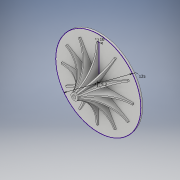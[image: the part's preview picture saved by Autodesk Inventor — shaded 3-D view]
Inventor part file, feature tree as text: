
AUTODESK INVENTOR PART (.ipt)
format: ipt  version: 2019.3 (Build 233278000, 278)  size: 221,696 bytes
history: native  units: mm
features: extrude x4, sketch x3, other x1, pattern_circular x1
ambient origin geometry x8: Origin, YZ Plane, XZ Plane, XY Plane, X Axis, Y Axis, Z Axis, Center Point
bodies: Solid1 (feature_tree)
feature tree (9):
  sketch  "Sketch1"  dims[d0=5.2mm d1=125.0mm]
  extrude  "Extrusion1"  Depth=125.0mm
  extrude  "Extrusion2"  Depth=2.0mm
  other  "Work Axis1"
  extrude  "Extrusion3"  Depth=10.0mm TaperAngle=0.0deg
  pattern_circular  "Circular Pattern1"  [2 undecoded]
  extrude  "Extrusion4"  Depth=2.0mm
  sketch  "Sketch2"  dims[d2=2.0mm d3=1.0mm]
  sketch  "Sketch3"  dims[d4=10.0mm d5=3.0mm d6=0.0mm d7=35.0mm d8=0.0mm d9=2.0mm d10=2.0mm d11=20.0mm d12=0.0mm d13=120.0mm d14=360.0deg d17=1.0mm d18=0.0mm d19=10.0mm d22=3.0mm d23=2.2mm]
note: 2 required parameter values undecoded (feature->parameter linkage not recoverable at this tier; creation-order binding heuristic only, values carry confidence <= 0.55)
